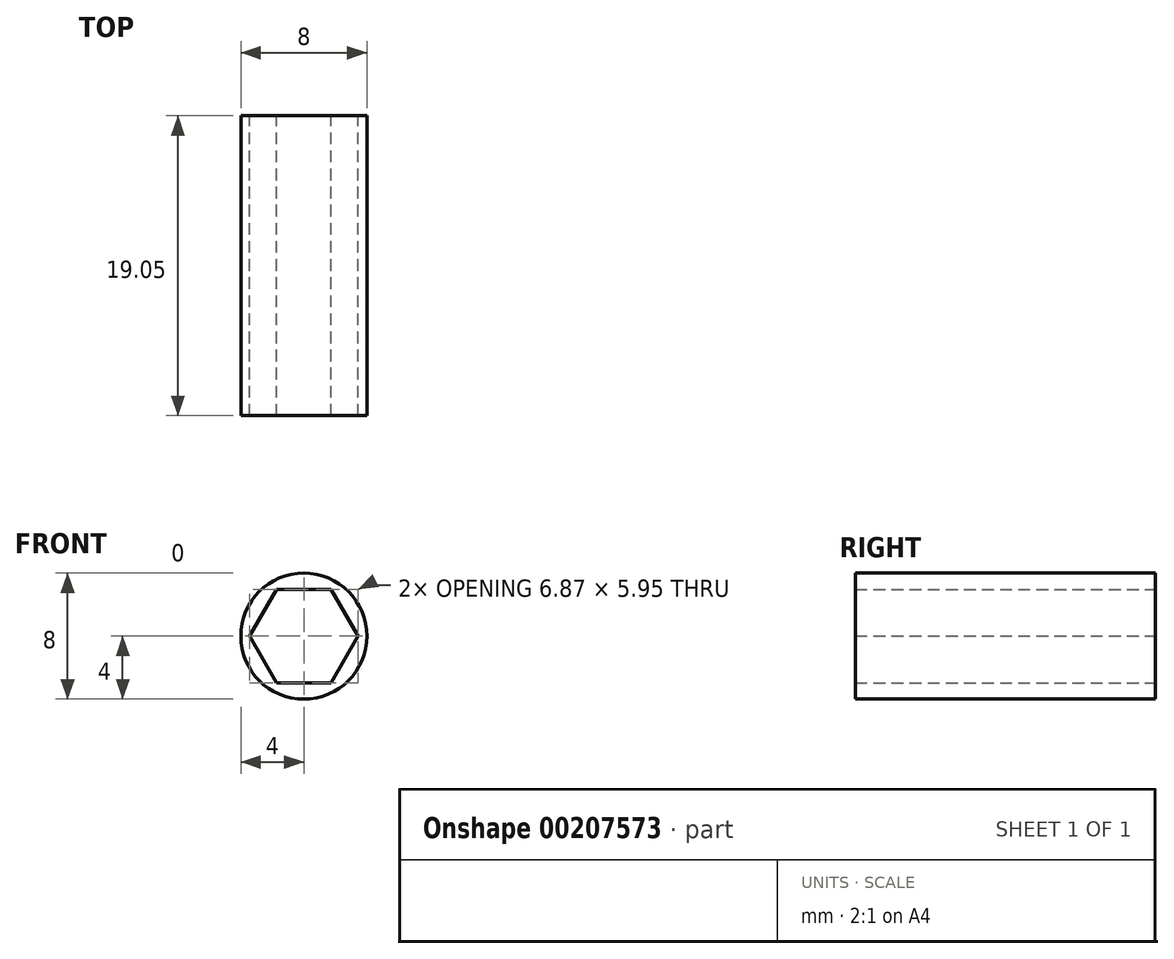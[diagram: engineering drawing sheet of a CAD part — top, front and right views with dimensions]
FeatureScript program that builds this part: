
annotation { "Feature Type Name" : "Feature", "Feature Type Description" : "" }
export const myFeature = defineFeature(function(context is Context, id is Id, definition is map)
    precondition{}
    {
        {
            var Q0;
            Q0=qCreatedBy(makeId("Front.planeOp"),FACE);
            var sketch = newSketch(context, id + "F0", { "sketchPlane" : qUnion([Q0])});
            skCircle(sketch, "E0.cCircle", {"center": v(0, 0) * mm, "radius": 2.98 * mm, "construction": true});
            skLineSegment(sketch, "E0.0", {"start": v(3.44, 0) * mm, "end": v(1.72, -2.98) * mm});
            skLineSegment(sketch, "E0.1", {"start": v(1.72, -2.98) * mm, "end": v(-1.72, -2.98) * mm});
            skLineSegment(sketch, "E0.2", {"start": v(-1.72, -2.97) * mm, "end": v(-3.44, 0) * mm});
            skLineSegment(sketch, "E0.3", {"start": v(-3.44, 0) * mm, "end": v(-1.72, 2.98) * mm});
            skLineSegment(sketch, "E0.4", {"start": v(-1.72, 2.98) * mm, "end": v(1.72, 2.98) * mm});
            skLineSegment(sketch, "E0.5", {"start": v(1.72, 2.98) * mm, "end": v(3.44, 0) * mm});
            skPoint(sketch, "E0.0.midPoint", {"position": v(2.58, -1.49) * mm});
            skLineSegment(sketch, "E1", {"start": v(0, 2.98) * mm, "end": v(0, -2.98) * mm, "construction": true});
            skCircle(sketch, "E2", {"center": v(0, 0) * mm, "radius": 4 * mm});
            skLineSegment(sketch, "E3", {"start": v(-3.44, 0) * mm, "end": v(3.44, 0) * mm, "construction": true});
            skSolve(sketch);
        }
        {
            var Q0;
            Q0=makeQuery(id+"F0.imprint","IMPRINT",FACE,{"disambiguationData":[TD([[makeQuery(id+"F0.imprint","IMPRINT",EDGE,{"derivedFrom":sQuery(id+"F0.wireOp",EDGE,"E0.0")}),1.0]])]});
            extrude(context, id + "F1", {"entities" : qUnion([Q0]), "depth" : 19.05 * mm});
        }
        {
            var Q0;
            Q0=makeQuery(id+"F1.opExtrude","SWEPT_BODY",BODY,{"disambiguationData":[OSD([sQuery(id+"F0.wireOp",EDGE,"E0.0"),sQuery(id+"F0.wireOp",EDGE,"E0.1"),sQuery(id+"F0.wireOp",EDGE,"E0.2"),sQuery(id+"F0.wireOp",EDGE,"E0.3"),sQuery(id+"F0.wireOp",EDGE,"E0.4"),sQuery(id+"F0.wireOp",EDGE,"E0.5"),sQuery(id+"F0.wireOp",EDGE,"E2")])]});
            transform(context, id + "F2", {"entities" : qUnion([Q0]), "transformType" : TransformType.TRANSLATION_3D, "dx" : 0 * mm, "dy" : 0 * mm, "dz" : 0 * mm, "makeCopy" : true});
        }
    });
